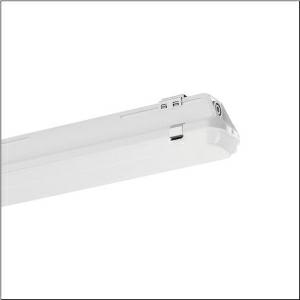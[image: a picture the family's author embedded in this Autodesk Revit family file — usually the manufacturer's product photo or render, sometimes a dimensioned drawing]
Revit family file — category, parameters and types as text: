
# Revit family: monsun_r__21_parking_51fg207p440b_4b42
name_source: partatom
category: Lighting Fixtures
units: mm (PartAtom-declared; Revit-internal decimal feet)

## family parameters
Cut with Voids When Loaded = No
Host = Face
Light Source = No
Part Type = Normal
Room Calculation Point = No
Round Connector Dimension = Use Diameter
Shared = No

## types (1)
- Monsun® 21 parking (1 x LED, 5050 lm, 35.4 W, 4000K)
    Apparent Load = 35 VA
    CIE Flux Codes = 45 75 93 94 100
    Color Rendering = 80
    Color Temperature = 4000K
    Default Elevation = 1800 mm
    Description = Monsun® 21 parking, damp-proof luminaire, chain hanger, primary optical cover: enclosure, of PC, light emission: direct distribution, primary light characteristic: symmetric, installation type: suspended mounting, surface-mounted, horizontal mounting, vertical mounting, LED, rated luminous flux: 5.050lm, luminous efficacy: 143lm/W, light colour: 840, colour temperature: 4000K, control gear: ECG, with terminal, 3-pole, max. 2.5mm², mains connection: 220..240V, AC, 50/60Hz, rated input power: 35W, housing, of glass-fibre reinforced polyester, uncoated, bright grey, length: 1.590mm, width: 90mm, height: 88mm, clip for enclosure, of stainless steel (V2A), ceiling mounting element, of stainless steel (V2A), chain hanger, of stainless steel (V2A), protection rating (complete): IP66, insulation class (complete): insulation class I (protective earthing), certification: CE, ENEC, VDE, UKCA, protection symbol: D, impact resistance: IK08, permissible operating ambient temperature: -25..+35°C, standard: EN 50419, EN 60598-2-1, corresponds to IFS (International Featured Standards) requirements for safety and quality in the food industry, for indoor or canopied outdoor use, no direct snow, no direct sun, no direct rain, packaging unit: 1 piece
    Height = 89 mm
    Lamp = 1 x LED
    Lamp Light Flux = 5050 lm
    Lamp Power = 35.4 W
    Lamp count = 1
    Length = 1590 mm
    Luminous efficacy = 143 lm/W
    Manufacturer = Siteco
    ModVariant = No
    Model = 51FG207P440B
    Mounting Place = Ceiling
    Mounting Type = Pendant
    Number of Poles = 1
    OnlyDefault = Yes
    Power Factor = 1
    Product Name = Monsun® 21 parking
    Product group = damp-proof luminaire | ceiling pendant
    ProductGroupID = 908
    Protection Class = Protection class I
    Protection Degree = IP 66
    RLX_Detail_Level = 1
    RlxData = <blob elided: 88189 chars, md5=d66c3589>
    Socket = socket
    Standby Power = 0 W
    System Light Flux = 5050 lm
    System Power = 35 W
    Type Comments = Product without accessories
    Type Image = l_1006717.jpg
    URL = http://relux.com
    VarID = ---
    Voltage = 0 V
    Weight = 0.00 kg
    Width = 90 mm

## geometry (parser evidence)
native form markers: Blend x4, Sweep x15
no freeform markers — native parametric forms only
